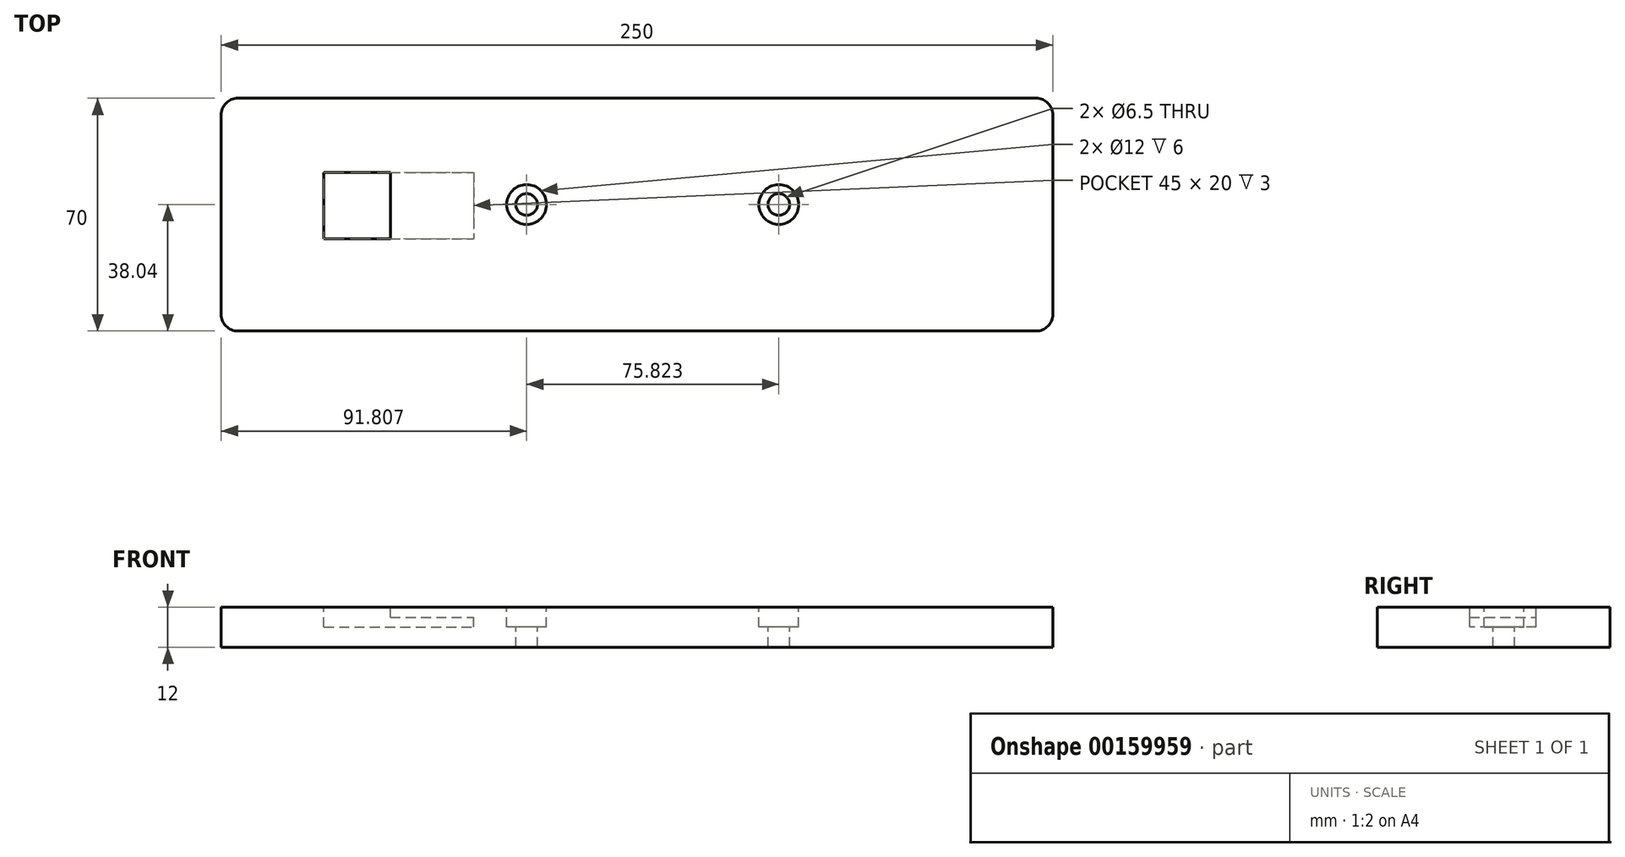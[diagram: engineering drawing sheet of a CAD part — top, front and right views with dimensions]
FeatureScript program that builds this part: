
annotation { "Feature Type Name" : "Feature", "Feature Type Description" : "" }
export const myFeature = defineFeature(function(context is Context, id is Id, definition is map)
    precondition{}
    {
        {
            var Q0;
            Q0=qCreatedBy(makeId("Top.planeOp"),FACE);
            var sketch = newSketch(context, id + "F0", { "sketchPlane" : qUnion([Q0])});
            skLineSegment(sketch, "E0.bottom", {"start": v(-128.65, 31.96) * mm, "end": v(121.35, 31.96) * mm});
            skLineSegment(sketch, "E0.top", {"start": v(-128.65, -38.04) * mm, "end": v(121.35, -38.04) * mm});
            skLineSegment(sketch, "E0.left", {"start": v(-128.65, 31.96) * mm, "end": v(-128.65, -38.04) * mm});
            skLineSegment(sketch, "E0.right", {"start": v(121.35, 31.96) * mm, "end": v(121.35, -38.04) * mm});
            skSolve(sketch);
        }
        {
            var Q0;
            Q0 = qSketchRegion(id + "F0", true);
            extrude(context, id + "F1", {"entities" : qUnion([Q0]), "depth" : 12 * mm});
        }
        {
            var Q0;
            Q0=makeQuery(id+"F1.opExtrude","CAP_FACE",FACE,{"disambiguationData":[OSD([sQuery(id+"F0.wireOp",EDGE,"E0.bottom"),sQuery(id+"F0.wireOp",EDGE,"E0.top"),sQuery(id+"F0.wireOp",EDGE,"E0.left"),sQuery(id+"F0.wireOp",EDGE,"E0.right")])],"isStart":false});
            var sketch = newSketch(context, id + "F2", { "sketchPlane" : qUnion([Q0])});
            skCircle(sketch, "E1", {"center": v(-36.84, 0) * mm, "radius": 3.25 * mm});
            skCircle(sketch, "E2", {"center": v(38.98, 0) * mm, "radius": 3.25 * mm});
            skSolve(sketch);
        }
        {
            var Q0;
            Q0 = qSketchRegion(id + "F2", true);
            extrude(context, id + "F3", {"entities" : qUnion([Q0]), "operationType" : NewBodyOperationType.REMOVE, "oppositeDirection" : true, "depth" : 25 * mm});
        }
        {
            var Q0;
            Q0=makeQuery(id+"F1.opExtrude","CAP_FACE",FACE,{"disambiguationData":[OSD([sQuery(id+"F0.wireOp",EDGE,"E0.bottom"),sQuery(id+"F0.wireOp",EDGE,"E0.top"),sQuery(id+"F0.wireOp",EDGE,"E0.left"),sQuery(id+"F0.wireOp",EDGE,"E0.right")])],"isStart":false});
            var sketch = newSketch(context, id + "F4", { "sketchPlane" : qUnion([Q0])});
            skCircle(sketch, "E3", {"center": v(-36.84, 0) * mm, "radius": 6 * mm});
            skCircle(sketch, "E4", {"center": v(38.98, 0) * mm, "radius": 6 * mm});
            skSolve(sketch);
        }
        {
            var Q0;
            Q0 = qSketchRegion(id + "F4", true);
            extrude(context, id + "F5", {"entities" : qUnion([Q0]), "operationType" : NewBodyOperationType.REMOVE, "oppositeDirection" : true, "depth" : 6 * mm});
        }
        {
            var Q0;
            Q0=makeQuery(id+"F1.opExtrude","CAP_FACE",FACE,{"disambiguationData":[OSD([sQuery(id+"F0.wireOp",EDGE,"E0.bottom"),sQuery(id+"F0.wireOp",EDGE,"E0.top"),sQuery(id+"F0.wireOp",EDGE,"E0.left"),sQuery(id+"F0.wireOp",EDGE,"E0.right")])],"isStart":false});
            var sketch = newSketch(context, id + "F6", { "sketchPlane" : qUnion([Q0])});
            skLineSegment(sketch, "E5.bottom", {"start": v(-97.78, 9.7) * mm, "end": v(-77.78, 9.7) * mm});
            skLineSegment(sketch, "E5.top", {"start": v(-97.78, -10.3) * mm, "end": v(-77.78, -10.3) * mm});
            skLineSegment(sketch, "E5.left", {"start": v(-97.78, 9.7) * mm, "end": v(-97.78, -10.3) * mm});
            skLineSegment(sketch, "E5.right", {"start": v(-77.78, 9.7) * mm, "end": v(-77.78, -10.3) * mm});
            skSolve(sketch);
        }
        {
            var Q0;
            Q0 = qSketchRegion(id + "F6", true);
            extrude(context, id + "F7", {"entities" : qUnion([Q0]), "operationType" : NewBodyOperationType.REMOVE, "oppositeDirection" : true, "depth" : 6 * mm});
        }
        {
            var Q0;
            Q0=makeQuery(id+"F7.boolean.opBoolean","COPY",FACE,{"derivedFrom":makeQuery(id+"F7.opExtrude","SWEPT_FACE",FACE,{"disambiguationData":[OSD([sQuery(id+"F6.wireOp",EDGE,"E5.right")])]})});
            var sketch = newSketch(context, id + "F8", { "sketchPlane" : qUnion([Q0])});
            skLineSegment(sketch, "E6.bottom", {"start": v(-9.7, 6) * mm, "end": v(10.3, 6) * mm});
            skLineSegment(sketch, "E6.top", {"start": v(-9.7, 9) * mm, "end": v(10.3, 9) * mm});
            skLineSegment(sketch, "E6.left", {"start": v(-9.7, 6) * mm, "end": v(-9.7, 9) * mm});
            skLineSegment(sketch, "E6.right", {"start": v(10.3, 6) * mm, "end": v(10.3, 9) * mm});
            skSolve(sketch);
        }
        {
            var Q0;
            Q0 = qSketchRegion(id + "F8", true);
            extrude(context, id + "F9", {"entities" : qUnion([Q0]), "operationType" : NewBodyOperationType.REMOVE, "depth" : 20 * mm, "hasSecondDirection" : true, "secondDirectionOppositeDirection" : true, "secondDirectionDepth" : 25 * mm});
        }
        {
            var Q0;
            Q0=makeQuery(id+"F1.opExtrude","SWEPT_EDGE",EDGE,{"disambiguationData":[OSD([sQuery(id+"F0.wireOp",EDGE,"E0.top"),sQuery(id+"F0.wireOp",EDGE,"E0.left")])]});
            var Q1;
            Q1=makeQuery(id+"F1.opExtrude","SWEPT_EDGE",EDGE,{"disambiguationData":[OSD([sQuery(id+"F0.wireOp",EDGE,"E0.bottom"),sQuery(id+"F0.wireOp",EDGE,"E0.left")])]});
            var Q2;
            Q2=makeQuery(id+"F1.opExtrude","SWEPT_EDGE",EDGE,{"disambiguationData":[OSD([sQuery(id+"F0.wireOp",EDGE,"E0.top"),sQuery(id+"F0.wireOp",EDGE,"E0.right")])]});
            var Q3;
            Q3=makeQuery(id+"F1.opExtrude","SWEPT_EDGE",EDGE,{"disambiguationData":[OSD([sQuery(id+"F0.wireOp",EDGE,"E0.bottom"),sQuery(id+"F0.wireOp",EDGE,"E0.right")])]});
            fillet(context, id + "F10", {"entities" : qUnion([Q0, Q1, Q2, Q3]), "radius" : 5 * mm, "tangentPropagation" : true, "allowEdgeOverflow" : false});
        }
    });
